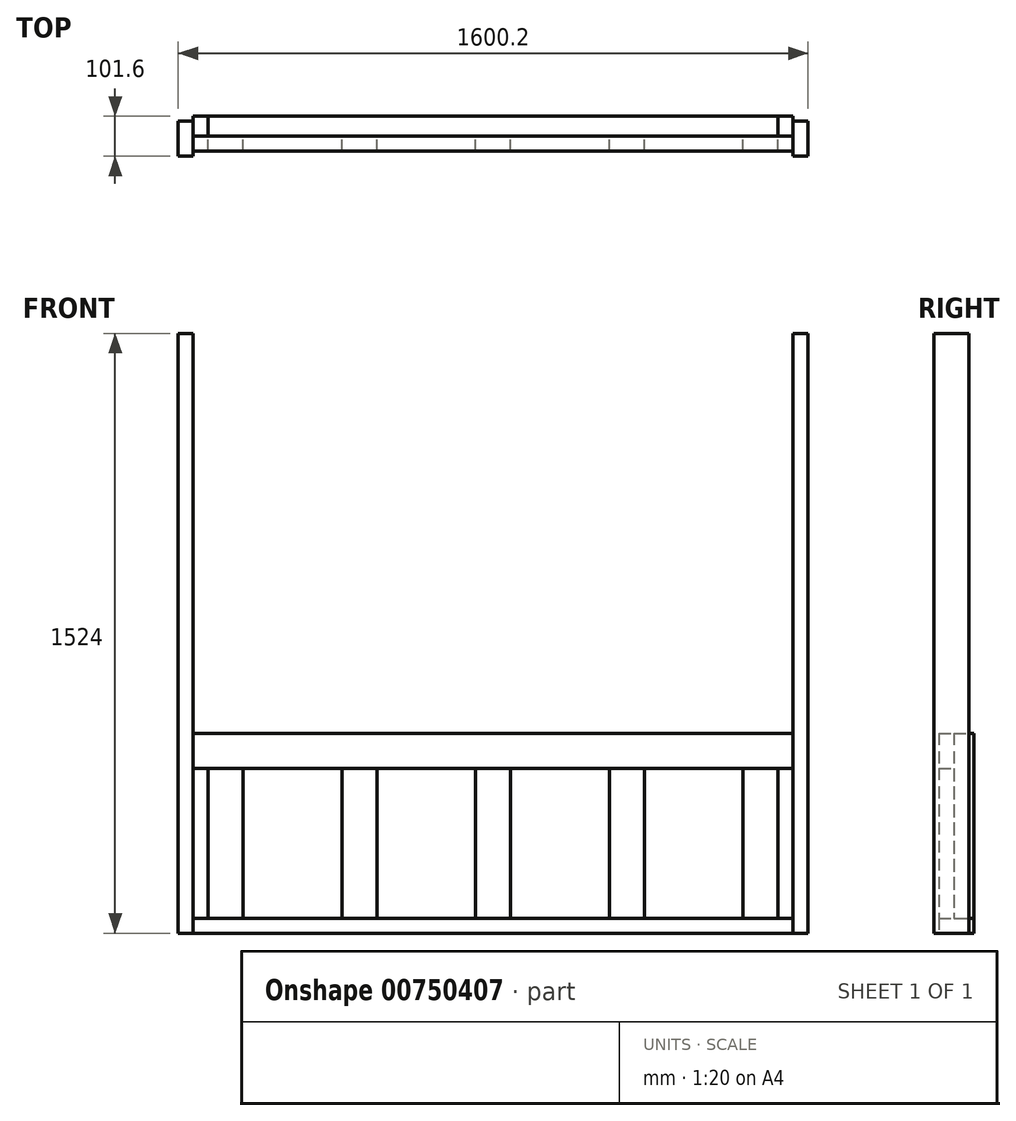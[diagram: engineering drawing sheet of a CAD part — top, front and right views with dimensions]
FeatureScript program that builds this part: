
annotation { "Feature Type Name" : "Feature", "Feature Type Description" : "" }
export const myFeature = defineFeature(function(context is Context, id is Id, definition is map)
    precondition{}
    {
        {
            var Q0;
            Q0=qCreatedBy(makeId("Top.planeOp"),FACE);
            var sketch = newSketch(context, id + "F0", { "sketchPlane" : qUnion([Q0])});
            skLineSegment(sketch, "E0.bottom", {"start": v(0, 0) * mm, "end": v(38.1, 0) * mm});
            skLineSegment(sketch, "E0.top", {"start": v(0, 88.9) * mm, "end": v(38.1, 88.9) * mm});
            skLineSegment(sketch, "E0.left", {"start": v(0, 0) * mm, "end": v(0, 88.9) * mm});
            skLineSegment(sketch, "E0.right", {"start": v(38.1, 0) * mm, "end": v(38.1, 88.9) * mm});
            skLineSegment(sketch, "E1.bottom", {"start": v(38.1, 0) * mm, "end": v(127, 0) * mm});
            skLineSegment(sketch, "E1.top", {"start": v(38.1, 38.1) * mm, "end": v(127, 38.1) * mm});
            skLineSegment(sketch, "E1.left", {"start": v(38.1, 0) * mm, "end": v(38.1, 38.1) * mm});
            skLineSegment(sketch, "E1.right", {"start": v(127, 0) * mm, "end": v(127, 38.1) * mm});
            skLineSegment(sketch, "E2.left", {"start": v(0, -12.7) * mm, "end": v(0, 76.2) * mm});
            skLineSegment(sketch, "E2.right", {"start": v(-38.1, -12.7) * mm, "end": v(-38.1, 76.2) * mm});
            skPoint(sketch, "E3.firstSnap0", {"position": v(82.55, 0) * mm});
            skLineSegment(sketch, "E3.bottom", {"start": v(1524, 0) * mm, "end": v(1485.9, 0) * mm});
            skLineSegment(sketch, "E3.top", {"start": v(1524, 88.9) * mm, "end": v(1485.9, 88.9) * mm});
            skLineSegment(sketch, "E3.left", {"start": v(1524, 0) * mm, "end": v(1524, 88.9) * mm});
            skLineSegment(sketch, "E3.right", {"start": v(1485.9, 0) * mm, "end": v(1485.9, 88.9) * mm});
            skLineSegment(sketch, "E4.left", {"start": v(1524, -12.7) * mm, "end": v(1524, 88.9) * mm});
            skLineSegment(sketch, "E4.right", {"start": v(1562.1, -12.7) * mm, "end": v(1562.1, 76.2) * mm});
            skLineSegment(sketch, "E5.bottom", {"start": v(1485.9, 0) * mm, "end": v(1397, 0) * mm});
            skLineSegment(sketch, "E5.top", {"start": v(1485.9, 38.1) * mm, "end": v(1397, 38.1) * mm});
            skLineSegment(sketch, "E5.left", {"start": v(1485.9, 0) * mm, "end": v(1485.9, 38.1) * mm});
            skLineSegment(sketch, "E5.right", {"start": v(1397, 0) * mm, "end": v(1397, 38.1) * mm});
            skLineSegment(sketch, "E6.bottom", {"start": v(377.83, 0) * mm, "end": v(466.73, 0) * mm});
            skLineSegment(sketch, "E6.top", {"start": v(377.83, 38.1) * mm, "end": v(466.73, 38.1) * mm});
            skLineSegment(sketch, "E6.left", {"start": v(377.83, 0) * mm, "end": v(377.83, 38.1) * mm});
            skLineSegment(sketch, "E6.right", {"start": v(466.73, 0) * mm, "end": v(466.73, 38.1) * mm});
            skLineSegment(sketch, "E7.bottom", {"start": v(717.55, 0) * mm, "end": v(806.45, 0) * mm});
            skLineSegment(sketch, "E7.top", {"start": v(717.55, 38.1) * mm, "end": v(806.45, 38.1) * mm});
            skLineSegment(sketch, "E7.left", {"start": v(717.55, 0) * mm, "end": v(717.55, 38.1) * mm});
            skLineSegment(sketch, "E7.right", {"start": v(806.45, 0) * mm, "end": v(806.45, 38.1) * mm});
            skLineSegment(sketch, "E8.bottom", {"start": v(1057.28, 0) * mm, "end": v(1146.18, 0) * mm});
            skLineSegment(sketch, "E8.top", {"start": v(1057.28, 38.1) * mm, "end": v(1146.18, 38.1) * mm});
            skLineSegment(sketch, "E8.left", {"start": v(1057.28, 0) * mm, "end": v(1057.28, 38.1) * mm});
            skLineSegment(sketch, "E8.right", {"start": v(1146.18, 0) * mm, "end": v(1146.18, 38.1) * mm});
            skPoint(sketch, "E9", {"position": v(762, 0) * mm});
            skLineSegment(sketch, "E10", {"start": v(127, 38.1) * mm, "end": v(377.83, 38.1) * mm});
            skLineSegment(sketch, "E11", {"start": v(127, 0) * mm, "end": v(377.83, 0) * mm});
            skLineSegment(sketch, "E12", {"start": v(466.73, 38.1) * mm, "end": v(717.55, 38.1) * mm});
            skLineSegment(sketch, "E13", {"start": v(466.73, 0) * mm, "end": v(717.55, 0) * mm});
            skLineSegment(sketch, "E14", {"start": v(806.45, 38.1) * mm, "end": v(1057.28, 38.1) * mm});
            skLineSegment(sketch, "E15", {"start": v(1057.28, 0) * mm, "end": v(806.45, 0) * mm});
            skLineSegment(sketch, "E16", {"start": v(1146.18, 38.1) * mm, "end": v(1397, 38.1) * mm});
            skLineSegment(sketch, "E17", {"start": v(1397, 0) * mm, "end": v(1146.18, 0) * mm});
            skLineSegment(sketch, "E18", {"start": v(1485.9, 88.9) * mm, "end": v(38.1, 88.9) * mm});
            skLineSegment(sketch, "E19", {"start": v(38.1, 38.1) * mm, "end": v(0, 38.1) * mm});
            skLineSegment(sketch, "E20", {"start": v(1485.9, 38.1) * mm, "end": v(1524, 38.1) * mm});
            skLineSegment(sketch, "E21.0", {"start": v(0, -12.7) * mm, "end": v(-38.1, -12.7) * mm});
            skLineSegment(sketch, "E22.0", {"start": v(0, 76.2) * mm, "end": v(-38.1, 76.2) * mm});
            skLineSegment(sketch, "E23.0", {"start": v(1524, -12.7) * mm, "end": v(1562.1, -12.7) * mm});
            skLineSegment(sketch, "E24.0", {"start": v(1524, 76.2) * mm, "end": v(1562.1, 76.2) * mm});
            skSolve(sketch);
        }
        {
            var Q0;
            Q0=makeQuery(id+"F0.imprint","IMPRINT",FACE,{"disambiguationData":[TD([[makeQuery(id+"F0.imprint","IMPRINT",EDGE,{"derivedFrom":sQuery(id+"F0.wireOp",EDGE,"E2.bottom")}),-1.0]])]});
            var Q1;
            Q1=makeQuery(id+"F0.imprint","IMPRINT",FACE,{"disambiguationData":[TD([[makeQuery(id+"F0.imprint","IMPRINT",EDGE,{"derivedFrom":sQuery(id+"F0.wireOp",EDGE,"E4.bottom")}),1.0]])]});
            var Q2;
            {var subQ0=sQuery(id+"F0.wireOp",EDGE,"E2.left");Q2=makeQuery(id+"F0.imprint","IMPRINT",FACE,{"disambiguationData":[TD([[makeQuery(id+"F0.imprint","IMPRINT",EDGE,{"derivedFrom":subQ0}),1.0]])]});}
            var Q3;
            {var subQ0=sQuery(id+"F0.wireOp",EDGE,"E4.left");Q3=makeQuery(id+"F0.imprint","IMPRINT",FACE,{"disambiguationData":[TD([[makeQuery(id+"F0.imprint","IMPRINT",EDGE,{"derivedFrom":subQ0}),-1.0]])]});}
            extrude(context, id + "F1", {"entities" : qUnion([Q0, Q1, Q2, Q3]), "depth" : 1524 * mm, "offsetDistance" : 25.4 * mm});
        }
        {
            var Q0;
            {var subQ0=sQuery(id+"F0.wireOp",EDGE,"E0.bottom");Q0=makeQuery(id+"F0.imprint","IMPRINT",FACE,{"disambiguationData":[TD([[makeQuery(id+"F0.imprint","IMPRINT",EDGE,{"derivedFrom":subQ0}),1.0]])]});}
            var Q1;
            {var subQ0=sQuery(id+"F0.wireOp",EDGE,"E1.bottom");Q1=makeQuery(id+"F0.imprint","IMPRINT",FACE,{"disambiguationData":[TD([[makeQuery(id+"F0.imprint","IMPRINT",EDGE,{"derivedFrom":subQ0}),1.0]])]});}
            var Q2;
            Q2=makeQuery(id+"F0.imprint","IMPRINT",FACE,{"disambiguationData":[TD([[makeQuery(id+"F0.imprint","IMPRINT",EDGE,{"derivedFrom":sQuery(id+"F0.wireOp",EDGE,"E1.right")}),-1.0]])]});
            var Q3;
            Q3=makeQuery(id+"F0.imprint","IMPRINT",FACE,{"disambiguationData":[TD([[makeQuery(id+"F0.imprint","IMPRINT",EDGE,{"derivedFrom":sQuery(id+"F0.wireOp",EDGE,"E6.bottom")}),1.0]])]});
            var Q4;
            Q4=makeQuery(id+"F0.imprint","IMPRINT",FACE,{"disambiguationData":[TD([[makeQuery(id+"F0.imprint","IMPRINT",EDGE,{"derivedFrom":sQuery(id+"F0.wireOp",EDGE,"E6.right")}),-1.0]])]});
            var Q5;
            Q5=makeQuery(id+"F0.imprint","IMPRINT",FACE,{"disambiguationData":[TD([[makeQuery(id+"F0.imprint","IMPRINT",EDGE,{"derivedFrom":sQuery(id+"F0.wireOp",EDGE,"E7.bottom")}),1.0]])]});
            var Q6;
            Q6=makeQuery(id+"F0.imprint","IMPRINT",FACE,{"disambiguationData":[TD([[makeQuery(id+"F0.imprint","IMPRINT",EDGE,{"derivedFrom":sQuery(id+"F0.wireOp",EDGE,"E7.right")}),-1.0]])]});
            var Q7;
            Q7=makeQuery(id+"F0.imprint","IMPRINT",FACE,{"disambiguationData":[TD([[makeQuery(id+"F0.imprint","IMPRINT",EDGE,{"derivedFrom":sQuery(id+"F0.wireOp",EDGE,"E8.bottom")}),1.0]])]});
            var Q8;
            Q8=makeQuery(id+"F0.imprint","IMPRINT",FACE,{"disambiguationData":[TD([[makeQuery(id+"F0.imprint","IMPRINT",EDGE,{"derivedFrom":sQuery(id+"F0.wireOp",EDGE,"E5.right")}),1.0]])]});
            var Q9;
            {var subQ0=sQuery(id+"F0.wireOp",EDGE,"E5.bottom");Q9=makeQuery(id+"F0.imprint","IMPRINT",FACE,{"disambiguationData":[TD([[makeQuery(id+"F0.imprint","IMPRINT",EDGE,{"derivedFrom":subQ0}),-1.0]])]});}
            var Q10;
            {var subQ0=sQuery(id+"F0.wireOp",EDGE,"E3.bottom");Q10=makeQuery(id+"F0.imprint","IMPRINT",FACE,{"disambiguationData":[TD([[makeQuery(id+"F0.imprint","IMPRINT",EDGE,{"derivedFrom":subQ0}),-1.0]])]});}
            extrude(context, id + "F2", {"entities" : qUnion([Q0, Q1, Q2, Q3, Q4, Q5, Q6, Q7, Q8, Q9, Q10]), "depth" : 508 * mm, "offsetDistance" : 25.4 * mm});
        }
        {
            var Q0;
            {var subQ0=sQuery(id+"F0.wireOp",EDGE,"E0.bottom");Q0=makeQuery(id+"F0.imprint","IMPRINT",FACE,{"disambiguationData":[TD([[makeQuery(id+"F0.imprint","IMPRINT",EDGE,{"derivedFrom":subQ0}),1.0]])]});}
            var Q1;
            {var subQ0=sQuery(id+"F0.wireOp",EDGE,"E1.bottom");Q1=makeQuery(id+"F0.imprint","IMPRINT",FACE,{"disambiguationData":[TD([[makeQuery(id+"F0.imprint","IMPRINT",EDGE,{"derivedFrom":subQ0}),1.0]])]});}
            var Q2;
            Q2=makeQuery(id+"F0.imprint","IMPRINT",FACE,{"disambiguationData":[TD([[makeQuery(id+"F0.imprint","IMPRINT",EDGE,{"derivedFrom":sQuery(id+"F0.wireOp",EDGE,"E1.right")}),-1.0]])]});
            var Q3;
            Q3=makeQuery(id+"F0.imprint","IMPRINT",FACE,{"disambiguationData":[TD([[makeQuery(id+"F0.imprint","IMPRINT",EDGE,{"derivedFrom":sQuery(id+"F0.wireOp",EDGE,"E6.bottom")}),1.0]])]});
            var Q4;
            Q4=makeQuery(id+"F0.imprint","IMPRINT",FACE,{"disambiguationData":[TD([[makeQuery(id+"F0.imprint","IMPRINT",EDGE,{"derivedFrom":sQuery(id+"F0.wireOp",EDGE,"E6.right")}),-1.0]])]});
            var Q5;
            Q5=makeQuery(id+"F0.imprint","IMPRINT",FACE,{"disambiguationData":[TD([[makeQuery(id+"F0.imprint","IMPRINT",EDGE,{"derivedFrom":sQuery(id+"F0.wireOp",EDGE,"E7.bottom")}),1.0]])]});
            var Q6;
            Q6=makeQuery(id+"F0.imprint","IMPRINT",FACE,{"disambiguationData":[TD([[makeQuery(id+"F0.imprint","IMPRINT",EDGE,{"derivedFrom":sQuery(id+"F0.wireOp",EDGE,"E7.right")}),-1.0]])]});
            var Q7;
            Q7=makeQuery(id+"F0.imprint","IMPRINT",FACE,{"disambiguationData":[TD([[makeQuery(id+"F0.imprint","IMPRINT",EDGE,{"derivedFrom":sQuery(id+"F0.wireOp",EDGE,"E8.bottom")}),1.0]])]});
            var Q8;
            Q8=makeQuery(id+"F0.imprint","IMPRINT",FACE,{"disambiguationData":[TD([[makeQuery(id+"F0.imprint","IMPRINT",EDGE,{"derivedFrom":sQuery(id+"F0.wireOp",EDGE,"E5.right")}),1.0]])]});
            var Q9;
            {var subQ0=sQuery(id+"F0.wireOp",EDGE,"E5.bottom");Q9=makeQuery(id+"F0.imprint","IMPRINT",FACE,{"disambiguationData":[TD([[makeQuery(id+"F0.imprint","IMPRINT",EDGE,{"derivedFrom":subQ0}),-1.0]])]});}
            var Q10;
            {var subQ0=sQuery(id+"F0.wireOp",EDGE,"E3.bottom");Q10=makeQuery(id+"F0.imprint","IMPRINT",FACE,{"disambiguationData":[TD([[makeQuery(id+"F0.imprint","IMPRINT",EDGE,{"derivedFrom":subQ0}),-1.0]])]});}
            extrude(context, id + "F3", {"entities" : qUnion([Q0, Q1, Q2, Q3, Q4, Q5, Q6, Q7, Q8, Q9, Q10]), "operationType" : NewBodyOperationType.REMOVE, "depth" : 419.1 * mm, "offsetDistance" : 25.4 * mm});
        }
        {
            var Q0;
            {var subQ1=sQuery(id+"F0.wireOp",EDGE,"E0.top");Q0=makeQuery(id+"F0.imprint","IMPRINT",FACE,{"disambiguationData":[TD([[makeQuery(id+"F0.imprint","IMPRINT",EDGE,{"derivedFrom":subQ1}),-1.0]])]});}
            var Q1;
            {var subQ1=sQuery(id+"F0.wireOp",EDGE,"E3.top");Q1=makeQuery(id+"F0.imprint","IMPRINT",FACE,{"disambiguationData":[TD([[makeQuery(id+"F0.imprint","IMPRINT",EDGE,{"derivedFrom":subQ1}),1.0]])]});}
            var Q2;
            Q2=makeQuery(id+"F2.opExtrude","CAP_FACE",FACE,{"disambiguationData":[OSD([sQuery(id+"F0.wireOp",EDGE,"E0.bottom"),sQuery(id+"F0.wireOp",EDGE,"E0.left"),sQuery(id+"F0.wireOp",EDGE,"E1.bottom"),sQuery(id+"F0.wireOp",EDGE,"E1.top"),sQuery(id+"F0.wireOp",EDGE,"E3.bottom"),sQuery(id+"F0.wireOp",EDGE,"E3.left"),sQuery(id+"F0.wireOp",EDGE,"E5.bottom"),sQuery(id+"F0.wireOp",EDGE,"E5.top"),sQuery(id+"F0.wireOp",EDGE,"E6.bottom"),sQuery(id+"F0.wireOp",EDGE,"E6.top"),sQuery(id+"F0.wireOp",EDGE,"E7.bottom"),sQuery(id+"F0.wireOp",EDGE,"E7.top"),sQuery(id+"F0.wireOp",EDGE,"E8.bottom"),sQuery(id+"F0.wireOp",EDGE,"E8.top"),sQuery(id+"F0.wireOp",EDGE,"E10"),sQuery(id+"F0.wireOp",EDGE,"E11"),sQuery(id+"F0.wireOp",EDGE,"E12"),sQuery(id+"F0.wireOp",EDGE,"E13"),sQuery(id+"F0.wireOp",EDGE,"E14"),sQuery(id+"F0.wireOp",EDGE,"E15"),sQuery(id+"F0.wireOp",EDGE,"E16"),sQuery(id+"F0.wireOp",EDGE,"E17"),sQuery(id+"F0.wireOp",EDGE,"E19"),sQuery(id+"F0.wireOp",EDGE,"E20")])],"isStart":false});
            extrude(context, id + "F4", {"entities" : qUnion([Q0, Q1]), "endBound" : BoundingType.UP_TO_SURFACE, "depth" : 25.4 * mm, "endBoundEntityFace" : qUnion([Q2]), "offsetDistance" : 25.4 * mm});
        }
        {
            var Q0;
            {var subQ0=sQuery(id+"F0.wireOp",EDGE,"E0.bottom");Q0=makeQuery(id+"F0.imprint","IMPRINT",FACE,{"disambiguationData":[TD([[makeQuery(id+"F0.imprint","IMPRINT",EDGE,{"derivedFrom":subQ0}),1.0]])]});}
            var Q1;
            {var subQ0=sQuery(id+"F0.wireOp",EDGE,"E3.bottom");Q1=makeQuery(id+"F0.imprint","IMPRINT",FACE,{"disambiguationData":[TD([[makeQuery(id+"F0.imprint","IMPRINT",EDGE,{"derivedFrom":subQ0}),-1.0]])]});}
            extrude(context, id + "F5", {"entities" : qUnion([Q0, Q1]), "endBound" : BoundingType.UP_TO_NEXT, "depth" : 25.4 * mm, "offsetDistance" : 25.4 * mm});
        }
        {
            var Q0;
            {var subQ0=sQuery(id+"F0.wireOp",EDGE,"E1.bottom");Q0=makeQuery(id+"F0.imprint","IMPRINT",FACE,{"disambiguationData":[TD([[makeQuery(id+"F0.imprint","IMPRINT",EDGE,{"derivedFrom":subQ0}),1.0]])]});}
            var Q1;
            Q1=makeQuery(id+"F0.imprint","IMPRINT",FACE,{"disambiguationData":[TD([[makeQuery(id+"F0.imprint","IMPRINT",EDGE,{"derivedFrom":sQuery(id+"F0.wireOp",EDGE,"E6.bottom")}),1.0]])]});
            var Q2;
            Q2=makeQuery(id+"F0.imprint","IMPRINT",FACE,{"disambiguationData":[TD([[makeQuery(id+"F0.imprint","IMPRINT",EDGE,{"derivedFrom":sQuery(id+"F0.wireOp",EDGE,"E7.bottom")}),1.0]])]});
            var Q3;
            Q3=makeQuery(id+"F0.imprint","IMPRINT",FACE,{"disambiguationData":[TD([[makeQuery(id+"F0.imprint","IMPRINT",EDGE,{"derivedFrom":sQuery(id+"F0.wireOp",EDGE,"E8.bottom")}),1.0]])]});
            var Q4;
            {var subQ0=sQuery(id+"F0.wireOp",EDGE,"E5.bottom");Q4=makeQuery(id+"F0.imprint","IMPRINT",FACE,{"disambiguationData":[TD([[makeQuery(id+"F0.imprint","IMPRINT",EDGE,{"derivedFrom":subQ0}),-1.0]])]});}
            var Q5;
            Q5=makeQuery(id+"F3.boolean.opBoolean","COPY",FACE,{"derivedFrom":makeQuery(id+"F3.opExtrude","CAP_FACE",FACE,{"disambiguationData":[OSD([sQuery(id+"F0.wireOp",EDGE,"E0.bottom"),sQuery(id+"F0.wireOp",EDGE,"E0.left"),sQuery(id+"F0.wireOp",EDGE,"E1.bottom"),sQuery(id+"F0.wireOp",EDGE,"E1.top"),sQuery(id+"F0.wireOp",EDGE,"E3.bottom"),sQuery(id+"F0.wireOp",EDGE,"E3.left"),sQuery(id+"F0.wireOp",EDGE,"E5.bottom"),sQuery(id+"F0.wireOp",EDGE,"E5.top"),sQuery(id+"F0.wireOp",EDGE,"E6.bottom"),sQuery(id+"F0.wireOp",EDGE,"E6.top"),sQuery(id+"F0.wireOp",EDGE,"E7.bottom"),sQuery(id+"F0.wireOp",EDGE,"E7.top"),sQuery(id+"F0.wireOp",EDGE,"E8.bottom"),sQuery(id+"F0.wireOp",EDGE,"E8.top"),sQuery(id+"F0.wireOp",EDGE,"E10"),sQuery(id+"F0.wireOp",EDGE,"E11"),sQuery(id+"F0.wireOp",EDGE,"E12"),sQuery(id+"F0.wireOp",EDGE,"E13"),sQuery(id+"F0.wireOp",EDGE,"E14"),sQuery(id+"F0.wireOp",EDGE,"E15"),sQuery(id+"F0.wireOp",EDGE,"E16"),sQuery(id+"F0.wireOp",EDGE,"E17"),sQuery(id+"F0.wireOp",EDGE,"E19"),sQuery(id+"F0.wireOp",EDGE,"E20")])],"isStart":false})});
            extrude(context, id + "F6", {"entities" : qUnion([Q0, Q1, Q2, Q3, Q4]), "endBound" : BoundingType.UP_TO_SURFACE, "depth" : 25.4 * mm, "endBoundEntityFace" : qUnion([Q5]), "offsetDistance" : 25.4 * mm});
        }
        {
            var Q0;
            {var subQ1=sQuery(id+"F0.wireOp",EDGE,"E3.top");Q0=makeQuery(id+"F0.imprint","IMPRINT",FACE,{"disambiguationData":[TD([[makeQuery(id+"F0.imprint","IMPRINT",EDGE,{"derivedFrom":subQ1}),1.0]])]});}
            var Q1;
            {var subQ0=sQuery(id+"F0.wireOp",EDGE,"E3.bottom");Q1=makeQuery(id+"F0.imprint","IMPRINT",FACE,{"disambiguationData":[TD([[makeQuery(id+"F0.imprint","IMPRINT",EDGE,{"derivedFrom":subQ0}),-1.0]])]});}
            var Q2;
            {var subQ0=sQuery(id+"F0.wireOp",EDGE,"E5.bottom");Q2=makeQuery(id+"F0.imprint","IMPRINT",FACE,{"disambiguationData":[TD([[makeQuery(id+"F0.imprint","IMPRINT",EDGE,{"derivedFrom":subQ0}),-1.0]])]});}
            var Q3;
            Q3=makeQuery(id+"F0.imprint","IMPRINT",FACE,{"disambiguationData":[TD([[makeQuery(id+"F0.imprint","IMPRINT",EDGE,{"derivedFrom":sQuery(id+"F0.wireOp",EDGE,"E8.bottom")}),1.0]])]});
            var Q4;
            Q4=makeQuery(id+"F0.imprint","IMPRINT",FACE,{"disambiguationData":[TD([[makeQuery(id+"F0.imprint","IMPRINT",EDGE,{"derivedFrom":sQuery(id+"F0.wireOp",EDGE,"E7.bottom")}),1.0]])]});
            var Q5;
            Q5=makeQuery(id+"F0.imprint","IMPRINT",FACE,{"disambiguationData":[TD([[makeQuery(id+"F0.imprint","IMPRINT",EDGE,{"derivedFrom":sQuery(id+"F0.wireOp",EDGE,"E6.bottom")}),1.0]])]});
            var Q6;
            {var subQ0=sQuery(id+"F0.wireOp",EDGE,"E1.bottom");Q6=makeQuery(id+"F0.imprint","IMPRINT",FACE,{"disambiguationData":[TD([[makeQuery(id+"F0.imprint","IMPRINT",EDGE,{"derivedFrom":subQ0}),1.0]])]});}
            var Q7;
            {var subQ0=sQuery(id+"F0.wireOp",EDGE,"E0.bottom");Q7=makeQuery(id+"F0.imprint","IMPRINT",FACE,{"disambiguationData":[TD([[makeQuery(id+"F0.imprint","IMPRINT",EDGE,{"derivedFrom":subQ0}),1.0]])]});}
            var Q8;
            {var subQ1=sQuery(id+"F0.wireOp",EDGE,"E0.top");Q8=makeQuery(id+"F0.imprint","IMPRINT",FACE,{"disambiguationData":[TD([[makeQuery(id+"F0.imprint","IMPRINT",EDGE,{"derivedFrom":subQ1}),-1.0]])]});}
            extrude(context, id + "F7", {"entities" : qUnion([Q0, Q1, Q2, Q3, Q4, Q5, Q6, Q7, Q8]), "operationType" : NewBodyOperationType.REMOVE, "depth" : 38.1 * mm, "offsetDistance" : 25.4 * mm});
        }
        {
            var Q0;
            {var subQ1=sQuery(id+"F0.wireOp",EDGE,"E3.top");Q0=makeQuery(id+"F0.imprint","IMPRINT",FACE,{"disambiguationData":[TD([[makeQuery(id+"F0.imprint","IMPRINT",EDGE,{"derivedFrom":subQ1}),1.0]])]});}
            var Q1;
            {var subQ0=sQuery(id+"F0.wireOp",EDGE,"E3.bottom");Q1=makeQuery(id+"F0.imprint","IMPRINT",FACE,{"disambiguationData":[TD([[makeQuery(id+"F0.imprint","IMPRINT",EDGE,{"derivedFrom":subQ0}),-1.0]])]});}
            var Q2;
            {var subQ0=sQuery(id+"F0.wireOp",EDGE,"E5.bottom");Q2=makeQuery(id+"F0.imprint","IMPRINT",FACE,{"disambiguationData":[TD([[makeQuery(id+"F0.imprint","IMPRINT",EDGE,{"derivedFrom":subQ0}),-1.0]])]});}
            var Q3;
            {var subQ4=sQuery(id+"F0.wireOp",EDGE,"E1.top");Q3=makeQuery(id+"F0.imprint","IMPRINT",FACE,{"disambiguationData":[TD([[makeQuery(id+"F0.imprint","IMPRINT",EDGE,{"derivedFrom":subQ4}),1.0]])]});}
            var Q4;
            Q4=makeQuery(id+"F0.imprint","IMPRINT",FACE,{"disambiguationData":[TD([[makeQuery(id+"F0.imprint","IMPRINT",EDGE,{"derivedFrom":sQuery(id+"F0.wireOp",EDGE,"E5.right")}),1.0]])]});
            var Q5;
            Q5=makeQuery(id+"F0.imprint","IMPRINT",FACE,{"disambiguationData":[TD([[makeQuery(id+"F0.imprint","IMPRINT",EDGE,{"derivedFrom":sQuery(id+"F0.wireOp",EDGE,"E8.bottom")}),1.0]])]});
            var Q6;
            Q6=makeQuery(id+"F0.imprint","IMPRINT",FACE,{"disambiguationData":[TD([[makeQuery(id+"F0.imprint","IMPRINT",EDGE,{"derivedFrom":sQuery(id+"F0.wireOp",EDGE,"E7.right")}),-1.0]])]});
            var Q7;
            Q7=makeQuery(id+"F0.imprint","IMPRINT",FACE,{"disambiguationData":[TD([[makeQuery(id+"F0.imprint","IMPRINT",EDGE,{"derivedFrom":sQuery(id+"F0.wireOp",EDGE,"E7.bottom")}),1.0]])]});
            var Q8;
            Q8=makeQuery(id+"F0.imprint","IMPRINT",FACE,{"disambiguationData":[TD([[makeQuery(id+"F0.imprint","IMPRINT",EDGE,{"derivedFrom":sQuery(id+"F0.wireOp",EDGE,"E6.right")}),-1.0]])]});
            var Q9;
            Q9=makeQuery(id+"F0.imprint","IMPRINT",FACE,{"disambiguationData":[TD([[makeQuery(id+"F0.imprint","IMPRINT",EDGE,{"derivedFrom":sQuery(id+"F0.wireOp",EDGE,"E6.bottom")}),1.0]])]});
            var Q10;
            Q10=makeQuery(id+"F0.imprint","IMPRINT",FACE,{"disambiguationData":[TD([[makeQuery(id+"F0.imprint","IMPRINT",EDGE,{"derivedFrom":sQuery(id+"F0.wireOp",EDGE,"E1.right")}),-1.0]])]});
            var Q11;
            {var subQ0=sQuery(id+"F0.wireOp",EDGE,"E1.bottom");Q11=makeQuery(id+"F0.imprint","IMPRINT",FACE,{"disambiguationData":[TD([[makeQuery(id+"F0.imprint","IMPRINT",EDGE,{"derivedFrom":subQ0}),1.0]])]});}
            var Q12;
            {var subQ1=sQuery(id+"F0.wireOp",EDGE,"E0.top");Q12=makeQuery(id+"F0.imprint","IMPRINT",FACE,{"disambiguationData":[TD([[makeQuery(id+"F0.imprint","IMPRINT",EDGE,{"derivedFrom":subQ1}),-1.0]])]});}
            var Q13;
            {var subQ0=sQuery(id+"F0.wireOp",EDGE,"E0.bottom");Q13=makeQuery(id+"F0.imprint","IMPRINT",FACE,{"disambiguationData":[TD([[makeQuery(id+"F0.imprint","IMPRINT",EDGE,{"derivedFrom":subQ0}),1.0]])]});}
            extrude(context, id + "F8", {"entities" : qUnion([Q0, Q1, Q2, Q3, Q4, Q5, Q6, Q7, Q8, Q9, Q10, Q11, Q12, Q13]), "depth" : 38.1 * mm, "offsetDistance" : 25.4 * mm});
        }
    });
